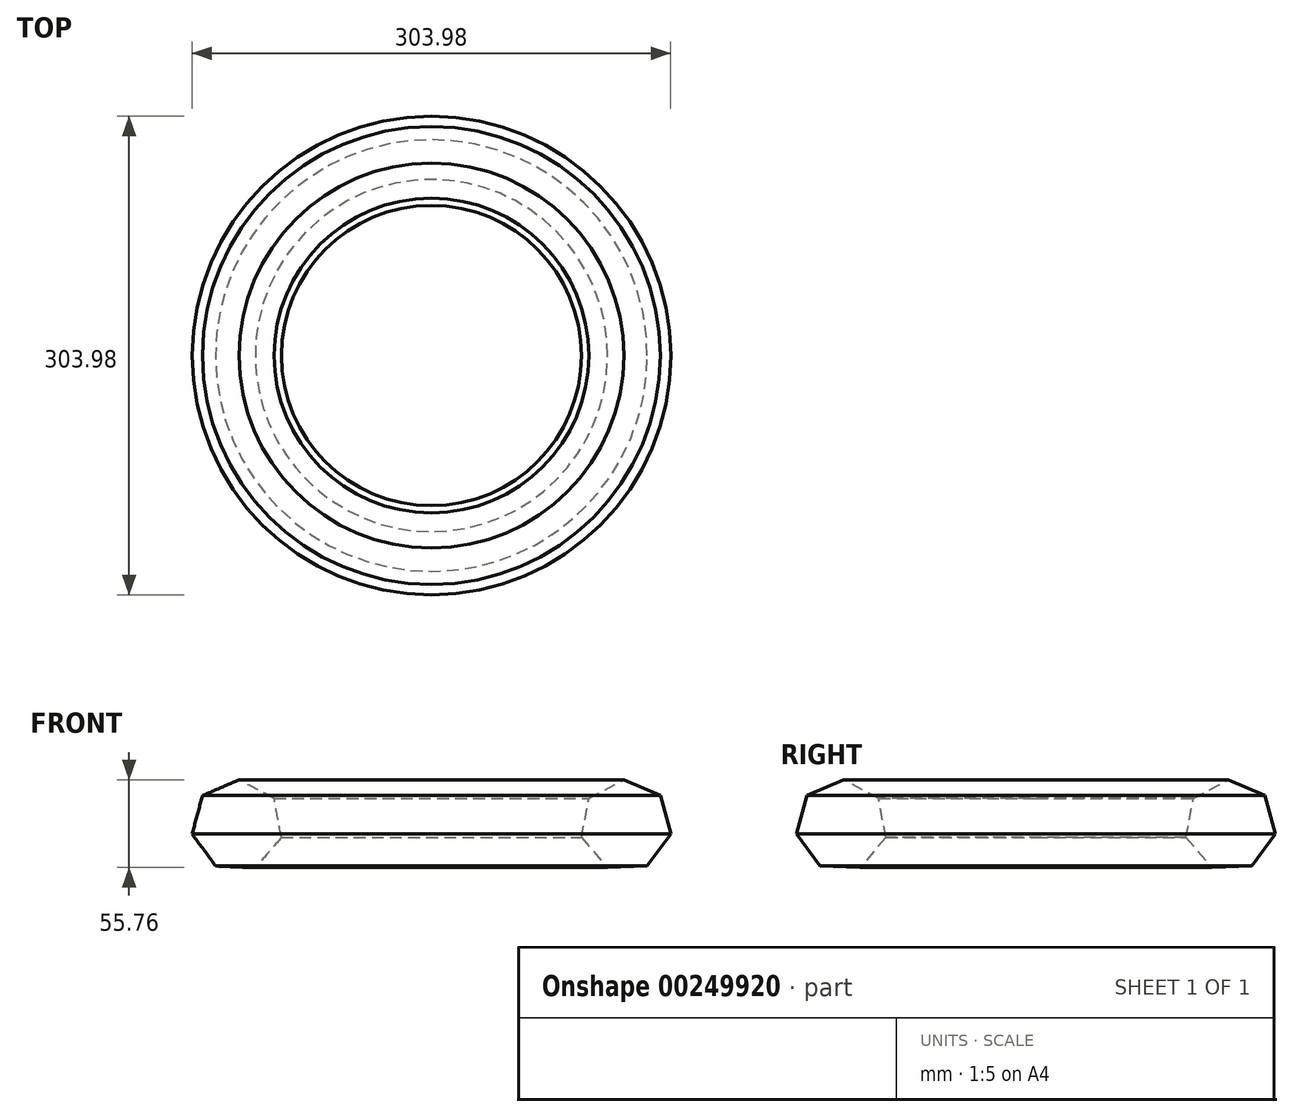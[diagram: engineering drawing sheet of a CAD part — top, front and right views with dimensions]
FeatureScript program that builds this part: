
annotation { "Feature Type Name" : "Feature", "Feature Type Description" : "" }
export const myFeature = defineFeature(function(context is Context, id is Id, definition is map)
    precondition{}
    {
        {
            var Q0;
            Q0=qCreatedBy(makeId("Front.planeOp"),FACE);
            var sketch = newSketch(context, id + "F0", { "sketchPlane" : qUnion([Q0])});
            skLineSegment(sketch, "E0", {"start": v(0, 0) * mm, "end": v(0, 122.88) * mm});
            skCircle(sketch, "E1.cCircle", {"center": v(-123.4, 31.45) * mm, "radius": 26.21 * mm, "construction": true});
            skLineSegment(sketch, "E1.0", {"start": v(-99.94, 48.67) * mm, "end": v(-95.31, 23.85) * mm});
            skLineSegment(sketch, "E1.1", {"start": v(-95.31, 23.85) * mm, "end": v(-111.83, 4.76) * mm});
            skLineSegment(sketch, "E1.2", {"start": v(-111.83, 4.76) * mm, "end": v(-137.06, 5.77) * mm});
            skLineSegment(sketch, "E1.3", {"start": v(-137.06, 5.77) * mm, "end": v(-152, 26.12) * mm});
            skLineSegment(sketch, "E1.4", {"start": v(-152, 26.12) * mm, "end": v(-145.4, 50.5) * mm});
            skLineSegment(sketch, "E1.5", {"start": v(-145.4, 50.5) * mm, "end": v(-122.23, 60.52) * mm});
            skLineSegment(sketch, "E1.6", {"start": v(-122.23, 60.52) * mm, "end": v(-99.94, 48.67) * mm});
            skPoint(sketch, "E1.0.midPoint", {"position": v(-97.63, 36.26) * mm});
            skSolve(sketch);
        }
        {
            var Q0;
            Q0=makeQuery(id+"F0.imprint","IMPRINT",FACE,{"disambiguationData":[TD([[makeQuery(id+"F0.imprint","IMPRINT",EDGE,{"derivedFrom":sQuery(id+"F0.wireOp",EDGE,"E1.0")}),-1.0]])]});
            var Q1;
            Q1=sQuery(id+"F0.wireOp",EDGE,"E0");
            revolve(context, id + "F1", {"entities" : qUnion([Q0]), "axis" : qUnion([Q1]), "revolveType" : RevolveType.FULL});
        }
    });
